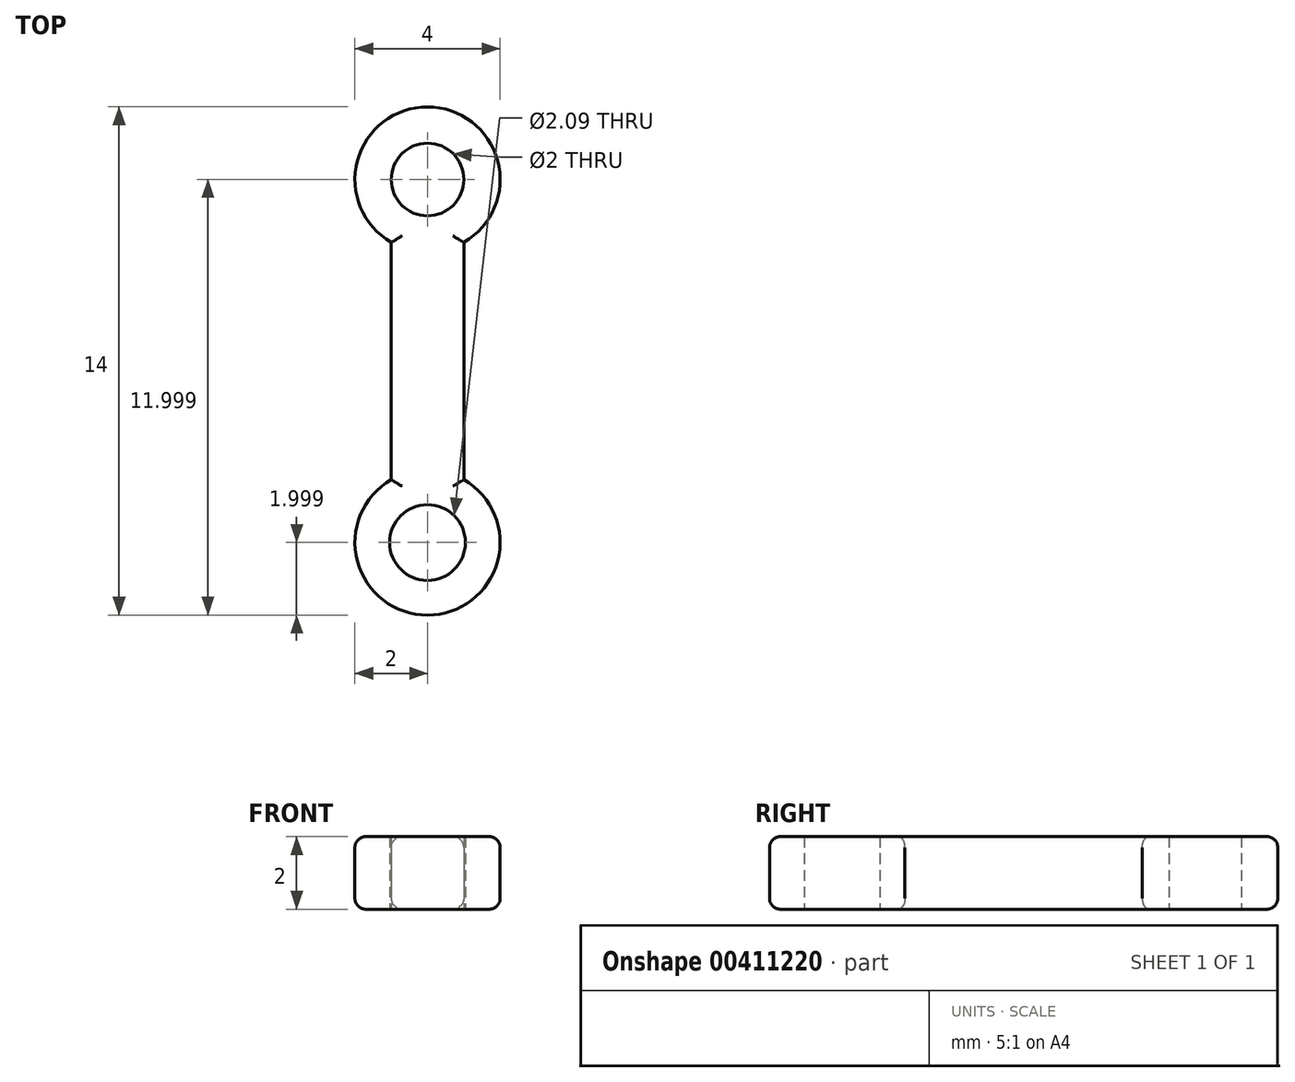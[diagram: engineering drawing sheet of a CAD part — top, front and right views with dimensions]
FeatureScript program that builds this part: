
annotation { "Feature Type Name" : "Feature", "Feature Type Description" : "" }
export const myFeature = defineFeature(function(context is Context, id is Id, definition is map)
    precondition{}
    {
        {
            var Q0;
            Q0=qCreatedBy(makeId("Top.planeOp"),FACE);
            var sketch = newSketch(context, id + "F0", { "sketchPlane" : qUnion([Q0])});
            skCircle(sketch, "E0", {"center": v(0, 5.73) * mm, "radius": 1 * mm});
            skCircle(sketch, "E1", {"center": v(0, -4.27) * mm, "radius": 1.04 * mm});
            skCircle(sketch, "E2", {"center": v(0, 5.73) * mm, "radius": 2 * mm});
            skCircle(sketch, "E3", {"center": v(0, -4.27) * mm, "radius": 2 * mm});
            skLineSegment(sketch, "E4", {"start": v(0, 3.73) * mm, "end": v(0, -2.27) * mm});
            skLineSegment(sketch, "E5", {"start": v(1, 0) * mm, "end": v(1, -2.54) * mm});
            skLineSegment(sketch, "E6", {"start": v(1, 0) * mm, "end": v(1, 4) * mm});
            skLineSegment(sketch, "E7", {"start": v(-1, 0) * mm, "end": v(-1, 4) * mm});
            skLineSegment(sketch, "E8", {"start": v(-1, 4) * mm, "end": v(-1, -2.54) * mm});
            skSolve(sketch);
        }
        {
            var Q0;
            Q0=makeQuery(id+"F0.imprint","IMPRINT",FACE,{"disambiguationData":[TD([[makeQuery(id+"F0.imprint","IMPRINT",EDGE,{"derivedFrom":sQuery(id+"F0.wireOp",EDGE,"E1")}),-1.0]])]});
            var Q1;
            {var subQ0=sQuery(id+"F0.wireOp",EDGE,"E4");Q1=makeQuery(id+"F0.imprint","IMPRINT",FACE,{"disambiguationData":[TD([[makeQuery(id+"F0.imprint","IMPRINT",EDGE,{"derivedFrom":subQ0}),-1.0]])]});}
            var Q2;
            {var subQ1=sQuery(id+"F0.wireOp",EDGE,"E4");Q2=makeQuery(id+"F0.imprint","IMPRINT",FACE,{"disambiguationData":[TD([[makeQuery(id+"F0.imprint","IMPRINT",EDGE,{"derivedFrom":subQ1}),1.0]])]});}
            var Q3;
            Q3=makeQuery(id+"F0.imprint","IMPRINT",FACE,{"disambiguationData":[TD([[makeQuery(id+"F0.imprint","IMPRINT",EDGE,{"derivedFrom":sQuery(id+"F0.wireOp",EDGE,"E0")}),-1.0]])]});
            extrude(context, id + "F1", {"entities" : qUnion([Q0, Q1, Q2, Q3]), "depth" : 2 * mm});
        }
        {
            var Q0;
            Q0=makeQuery(id+"F1.opExtrude","CAP_EDGE",EDGE,{"disambiguationData":[OSD([sQuery(id+"F0.wireOp",EDGE,"E5"),sQuery(id+"F0.wireOp",EDGE,"E6")])],"isStart":false});
            var Q1;
            Q1=makeQuery(id+"F1.opExtrude","CAP_EDGE",EDGE,{"disambiguationData":[OSD([sQuery(id+"F0.wireOp",EDGE,"E5"),sQuery(id+"F0.wireOp",EDGE,"E6")])],"isStart":true});
            var Q2;
            Q2=makeQuery(id+"F1.opExtrude","CAP_EDGE",EDGE,{"disambiguationData":[OSD([sQuery(id+"F0.wireOp",EDGE,"E8")])],"isStart":true});
            var Q3;
            Q3=makeQuery(id+"F1.opExtrude","CAP_EDGE",EDGE,{"disambiguationData":[OSD([sQuery(id+"F0.wireOp",EDGE,"E8")])],"isStart":false});
            fillet(context, id + "F2", {"entities" : qUnion([Q0, Q1, Q2, Q3]), "radius" : 0.3 * mm, "tangentPropagation" : true, "allowEdgeOverflow" : false});
        }
        {
            var Q0;
            Q0=makeQuery(id+"F1.opExtrude","CAP_EDGE",EDGE,{"disambiguationData":[OSD([sQuery(id+"F0.wireOp",EDGE,"E2")])],"isStart":false});
            var Q1;
            Q1=makeQuery(id+"F1.opExtrude","CAP_EDGE",EDGE,{"disambiguationData":[OSD([sQuery(id+"F0.wireOp",EDGE,"E2")])],"isStart":true});
            var Q2;
            Q2=makeQuery(id+"F1.opExtrude","CAP_EDGE",EDGE,{"disambiguationData":[OSD([sQuery(id+"F0.wireOp",EDGE,"E3")])],"isStart":true});
            var Q3;
            Q3=makeQuery(id+"F1.opExtrude","CAP_EDGE",EDGE,{"disambiguationData":[OSD([sQuery(id+"F0.wireOp",EDGE,"E3")])],"isStart":false});
            fillet(context, id + "F3", {"entities" : qUnion([Q0, Q1, Q2, Q3]), "radius" : 0.3 * mm, "tangentPropagation" : true, "allowEdgeOverflow" : false});
        }
    });
